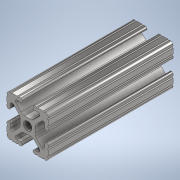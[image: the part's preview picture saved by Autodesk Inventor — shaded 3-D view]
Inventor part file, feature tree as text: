
AUTODESK INVENTOR PART (.ipt)
format: ipt  version: 2020 (Build 240168000, 168)  size: 244,736 bytes
history: native  units: in
note: dims shown in document units (in); Inventor stores cm internally (conversion verified against a paired STEP export)
features: extrude x1, sketch x1
ambient origin geometry x8: Origin, YZ Plane, XZ Plane, XY Plane, X Axis, Y Axis, Z Axis, Center Point
bodies: Solid1 (feature_tree)
feature tree (2):
  extrude  "Extrusion1"  [1 undecoded]
  sketch  "Sketch1"  dims[d0=3.0in d1=0.0in]
note: 1 required parameter value undecoded (feature->parameter linkage not recoverable at this tier; creation-order binding heuristic only, values carry confidence <= 0.55)
